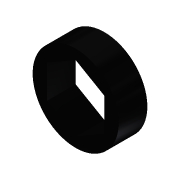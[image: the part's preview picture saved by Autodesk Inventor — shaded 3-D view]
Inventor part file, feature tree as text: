
AUTODESK INVENTOR PART (.ipt)
format: ipt  version: 2015 (Build 190159000, 159)  size: 82,432 bytes
history: native  units: in
note: dims shown in document units (in); Inventor stores cm internally (conversion verified against a paired STEP export)
features: extrude x1, sketch x1
ambient origin geometry x8: Origin, YZ Plane, XZ Plane, XY Plane, X Axis, Y Axis, Z Axis, Center Point
bodies: Solid1 (feature_tree)
feature tree (2):
  extrude  "Extrusion1"  Depth=0.5in
  sketch  "Sketch1"  dims[d0=0.75in d1=0.5in d2=0.25in d3=0.0in]
